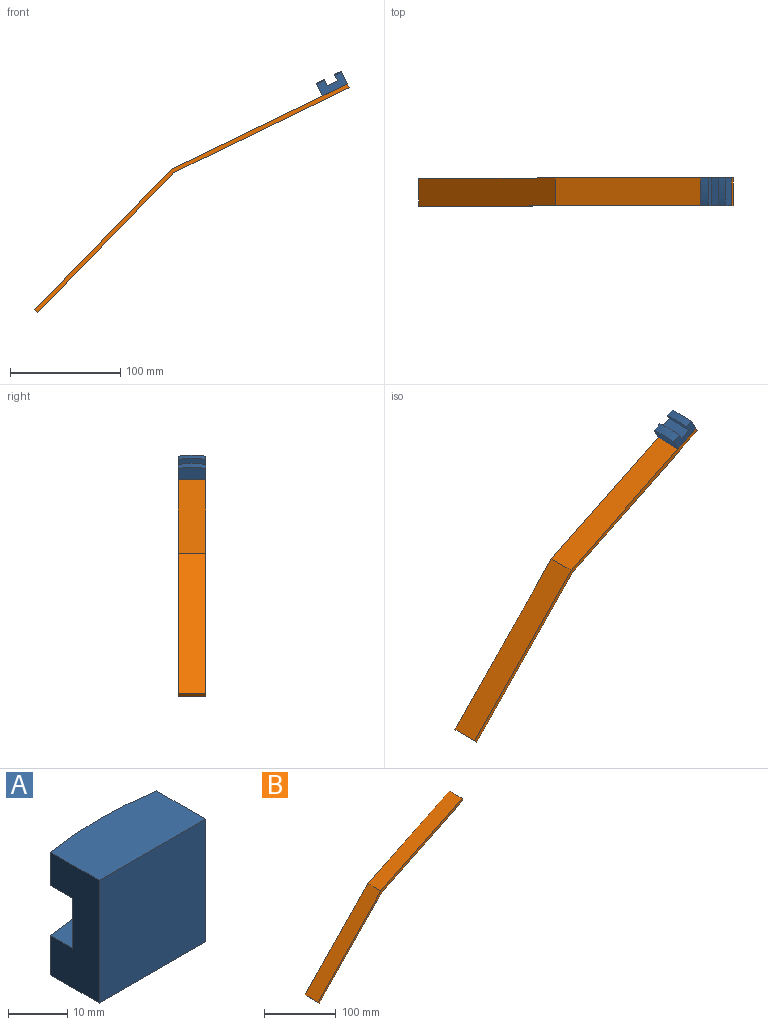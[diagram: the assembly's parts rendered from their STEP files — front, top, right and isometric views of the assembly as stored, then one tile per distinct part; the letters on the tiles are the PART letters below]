
ASSEMBLY  parts=2 mates=1
PART A: 10 faces, bbox 25.4x12.7x25.4 mm
  f0: cylinder r=76.2mm len=25.4mm, axis (0,0,-1), area 175mm2, adj f2,f3,f5,f7
  f1: cylinder r=76.2mm len=25.4mm, axis (0,0,-1), area 208.2mm2, adj f2,f3,f6,f8
  f2: plane 25.4x11.63mm, normal (-1,0,0), area 240.6mm2, adj f0,f1,f4,f5,f6,f7,f8,f9
  f3: plane 25.4x11.63mm, normal (1,0,0), area 240.6mm2, adj f0,f1,f4,f5,f6,f7,f8,f9
  f4: plane 25.4x25.4mm, normal (0,-1,0), area 645.2mm2, adj f2,f3,f5,f6
  f5: plane 25.4x12.7mm, normal (0,0,1), area 313.6mm2, adj f0,f2,f3,f4
  f6: plane 25.4x12.7mm, normal (0,0,-1), area 313.6mm2, adj f1,f2,f3,f4
  f7: plane 25.4x6.35mm, normal (0,0,-1), area 152.3mm2, adj f0,f2,f3,f9
  f8: plane 25.4x6.35mm, normal (0,0,1), area 152.3mm2, adj f1,f2,f3,f9
  f9: plane 25.4x10.38mm, normal (0,1,0), area 263.7mm2, adj f2,f3,f7,f8
PART B: 8 faces, bbox 285.4x25.4x207.9 mm
  f0: plane 127.66x123.76mm, normal (-0.72,0,0.7), area 4516.1mm2, adj f1,f5,f6,f7
  f1: plane 25.4x2.74mm, normal (-0.7,0,-0.72), area 96.8mm2, adj f0,f2,f6,f7
  f2: plane 126.88x122.69mm, normal (0.72,0,-0.7), area 4483mm2, adj f1,f3,f6,f7
  f3: plane 159.96x77.63mm, normal (0.44,0,-0.9), area 4516.1mm2, adj f2,f4,f6,f7
  f4: plane 25.4x3.43mm, normal (0.9,0,0.44), area 96.8mm2, adj f3,f5,f6,f7
  f5: plane 159.96x77.63mm, normal (-0.44,0,0.9), area 4516.1mm2, adj f0,f4,f6,f7
  f6: plane 285.38x207.94mm, normal (0,-1,0), area 1331.9mm2, adj f0,f1,f2,f3,f4,f5
  f7: plane 285.38x207.94mm, normal (0,1,0), area 1331.9mm2, adj f0,f1,f2,f3,f4,f5
PLACE A rot(axis=(0.47,0.47,0.75),106.4deg) t=(95.7,8.42,124.58)mm
PLACE B t=(-14.05,21.12,11.18)mm
MATE fastened A.f4 <-> B.f5  axis (0.44,0,-0.9) through (124.1,8.42,124.24)mm
